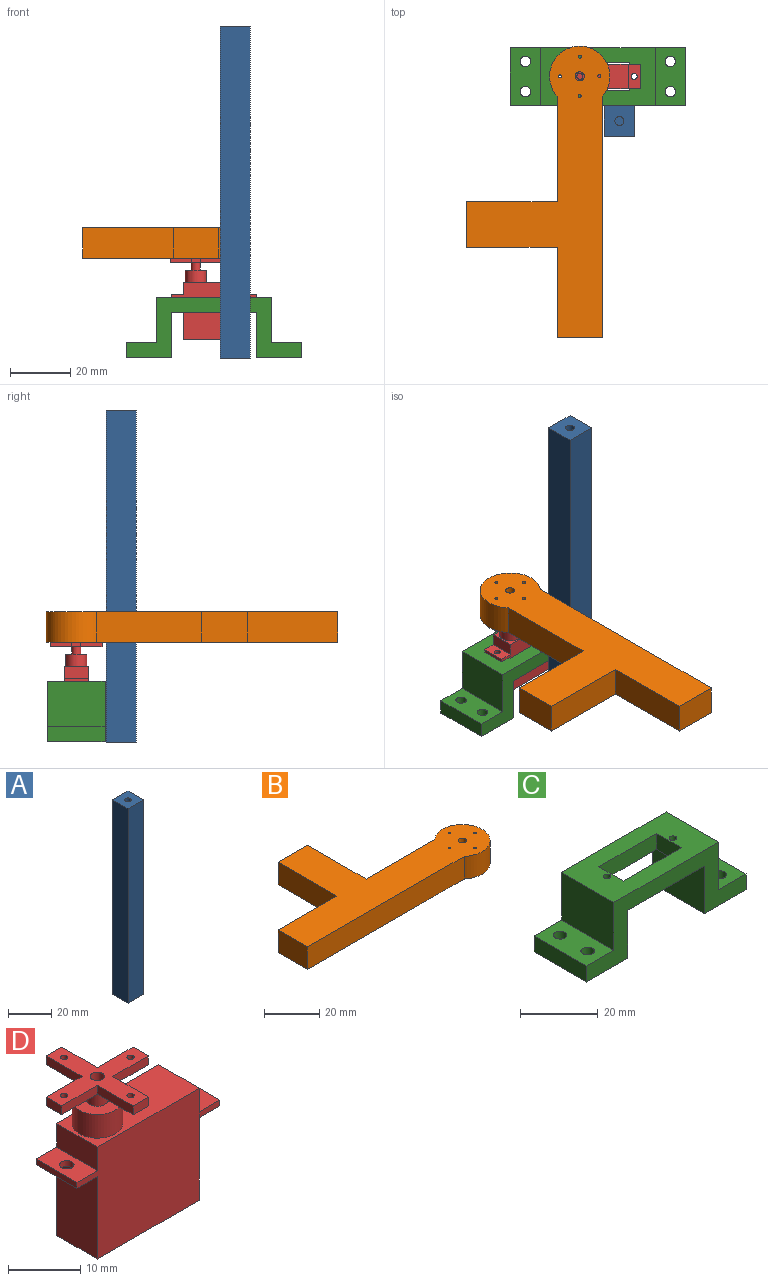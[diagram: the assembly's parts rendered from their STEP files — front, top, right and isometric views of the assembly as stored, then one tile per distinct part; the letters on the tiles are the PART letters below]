
ASSEMBLY  parts=4 mates=2
PART A: 10 faces, bbox 10x10x110 mm
  f0: plane 110x10mm, normal (1,0,0), area 1100mm2, adj f1,f3,f4,f5
  f1: plane 110x10mm, normal (0,1,0), area 1100mm2, adj f0,f2,f4,f5
  f2: plane 110x10mm, normal (-1,0,0), area 1100mm2, adj f1,f3,f4,f5
  f3: plane 110x10mm, normal (0,-1,0), area 1100mm2, adj f0,f2,f4,f5
  f4: plane 10x10mm, normal (0,0,1), area 92.9mm2, adj f0,f1,f2,f3,f8
  f5: plane 10x10mm, normal (0,0,-1), area 92.9mm2, adj f0,f1,f2,f3,f6
  f6: cylinder r=1.5mm len=20mm, axis (0,0,-1), area 188.5mm2, adj f5,f7
  f7: plane 3x3mm, normal (0,0,-1), area 7.1mm2, adj f6
  f8: cylinder r=1.5mm len=30mm, axis (0,0,1), area 282.7mm2, adj f4,f9
  f9: plane 3x3mm, normal (0,0,1), area 7.1mm2, adj f8
PART B: 15 faces, bbox 96.6x47.5x10 mm
  f0: cylinder r=10mm len=20mm, axis (0,0,-1), area 458.7mm2, adj f1,f12,f13,f14
  f1: plane 35x10mm, normal (0,1,0), area 350mm2, adj f0,f2,f13,f14
  f2: plane 30x10mm, normal (1,0,0), area 300mm2, adj f1,f3,f13,f14
  f3: plane 15x10mm, normal (0,1,0), area 150mm2, adj f2,f4,f13,f14
  f4: plane 30x10mm, normal (-1,0,0), area 300mm2, adj f3,f5,f13,f14
  f5: plane 30x10mm, normal (0,1,0), area 300mm2, adj f4,f6,f13,f14
  f6: plane 15x10mm, normal (-1,0,0), area 150mm2, adj f5,f12,f13,f14
  f7: cylinder r=1.5mm len=10mm, axis (0,0,-1), area 94.2mm2, adj f13,f14
  f8: cylinder r=0.5mm len=10mm, axis (0,0,-1), area 31.4mm2, adj f13,f14
  f9: cylinder r=0.5mm len=10mm, axis (0,0,-1), area 31.4mm2, adj f13,f14
  f10: cylinder r=0.5mm len=10mm, axis (0,0,-1), area 31.4mm2, adj f13,f14
  f11: cylinder r=0.5mm len=10mm, axis (0,0,-1), area 31.4mm2, adj f13,f14
  f12: plane 80x10mm, normal (0,-1,0), area 800mm2, adj f0,f6,f13,f14
  f13: plane 96.61x47.5mm, normal (0,0,1), area 1918.8mm2, adj f0,f1,f2,f3,f4,f5,f6,f7
  f14: plane 96.61x47.5mm, normal (0,0,-1), area 1918.8mm2, adj f0,f1,f2,f3,f4,f5,f6,f7
PART C: 24 faces, bbox 58x19x20 mm
  f0: plane 28x19mm, normal (0,0,-1), area 336.7mm2, adj f6,f7,f12,f13,f14,f15,f16,f17
  f1: plane 38x19mm, normal (0,0,1), area 526.7mm2, adj f2,f11,f12,f13,f14,f15,f16,f17
  f2: plane 19x15mm, normal (-1,0,0), area 285mm2, adj f1,f3,f12,f13
  f3: plane 19x10mm, normal (0,0,1), area 170.8mm2, adj f2,f4,f12,f13,f22,f23
  f4: plane 19x5mm, normal (-1,0,0), area 95mm2, adj f3,f5,f12,f13
  f5: plane 19x15mm, normal (0,0,-1), area 265.8mm2, adj f4,f6,f12,f13,f22,f23
  f6: plane 19x15mm, normal (1,0,0), area 285mm2, adj f0,f5,f12,f13
  f7: plane 19x15mm, normal (-1,0,0), area 285mm2, adj f0,f8,f12,f13
  f8: plane 19x15mm, normal (0,0,-1), area 265.8mm2, adj f7,f9,f12,f13,f20,f21
  f9: plane 19x5mm, normal (1,0,0), area 95mm2, adj f8,f10,f12,f13
  f10: plane 19x10mm, normal (0,0,1), area 170.8mm2, adj f9,f11,f12,f13,f20,f21
  f11: plane 19x15mm, normal (1,0,0), area 285mm2, adj f1,f10,f12,f13
  f12: plane 58x20mm, normal (0,-1,0), area 440mm2, adj f0,f1,f2,f3,f4,f5,f6,f7
  f13: plane 58x20mm, normal (0,1,0), area 440mm2, adj f0,f1,f2,f3,f4,f5,f6,f7
  f14: plane 9x5mm, normal (-1,0,0), area 45mm2, adj f0,f1,f15,f17
  f15: plane 21x5mm, normal (0,-1,0), area 105mm2, adj f0,f1,f14,f16
  f16: plane 9x5mm, normal (1,0,0), area 45mm2, adj f0,f1,f15,f17
  f17: plane 21x5mm, normal (0,1,0), area 105mm2, adj f0,f1,f14,f16
  f18: cylinder r=1mm len=5mm, axis (0,0,1), area 31.4mm2, adj f0,f1
  f19: cylinder r=1mm len=5mm, axis (0,0,1), area 31.4mm2, adj f0,f1
  f20: cylinder r=1.75mm len=5mm, axis (0,0,1), area 55mm2, adj f8,f10
  f21: cylinder r=1.75mm len=5mm, axis (0,0,1), area 55mm2, adj f8,f10
  f22: cylinder r=1.75mm len=5mm, axis (0,0,1), area 55mm2, adj f3,f5
  f23: cylinder r=1.75mm len=5mm, axis (0,0,1), area 55mm2, adj f3,f5
PART D: 41 faces, bbox 28.5x17x27 mm
  f0: plane 8x4mm, normal (-1,0,0), area 32mm2, adj f3,f5,f6,f16
  f1: plane 14x8mm, normal (1,0,0), area 112mm2, adj f3,f5,f7,f11
  f2: plane 14x8mm, normal (-1,0,0), area 112mm2, adj f3,f5,f7,f15
  f3: plane 24x19mm, normal (0,-1,0), area 384mm2, adj f0,f1,f2,f4,f6,f7,f10,f15
  f4: plane 8x4mm, normal (1,0,0), area 32mm2, adj f3,f5,f6,f13
  f5: plane 24x19mm, normal (0,1,0), area 384mm2, adj f0,f1,f2,f4,f6,f7,f12,f15
  f6: plane 20x8mm, normal (0,0,1), area 121.5mm2, adj f0,f3,f4,f5,f8
  f7: plane 20x8mm, normal (0,0,-1), area 160mm2, adj f1,f2,f3,f5
  f8: cylinder r=3.5mm len=7mm, axis (0,0,-1), area 88mm2, adj f6,f9
  f9: plane 7x7mm, normal (0,0,1), area 31.4mm2, adj f8,f18
  f10: plane 4x1mm, normal (0,-1,0), area 4mm2, adj f3,f11,f13,f14
  f11: plane 8x4mm, normal (0,0,-1), area 28.9mm2, adj f1,f10,f12,f14,f20
  f12: plane 4x1mm, normal (0,1,0), area 4mm2, adj f5,f11,f13,f14
  f13: plane 8x4mm, normal (0,0,1), area 28.9mm2, adj f4,f10,f12,f14,f20
  f14: plane 8x1mm, normal (1,0,0), area 8mm2, adj f10,f11,f12,f13
  f15: plane 8x4mm, normal (0,0,-1), area 28.9mm2, adj f2,f3,f5,f17,f19
  f16: plane 8x4mm, normal (0,0,1), area 28.9mm2, adj f0,f3,f5,f17,f19
  f17: plane 8x1mm, normal (-1,0,0), area 8mm2, adj f3,f5,f15,f16
  f18: cylinder r=1.5mm len=3mm, axis (0,0,-1), area 23.6mm2, adj f9,f34
  f19: cylinder r=1mm len=2mm, axis (0,0,1), area 6.3mm2, adj f15,f16
  f20: cylinder r=1mm len=2mm, axis (0,0,1), area 6.3mm2, adj f11,f13
  f21: plane 7x1.5mm, normal (0,1,0), area 10.5mm2, adj f22,f32,f33,f34
  f22: plane 3x1.5mm, normal (-1,0,0), area 4.5mm2, adj f21,f23,f33,f34
  f23: plane 7x1.5mm, normal (0,-1,0), area 10.5mm2, adj f22,f24,f33,f34
  f24: plane 7x1.5mm, normal (-1,0,0), area 10.5mm2, adj f23,f25,f33,f34
  f25: plane 3x1.5mm, normal (0,-1,0), area 4.5mm2, adj f24,f26,f33,f34
  f26: plane 7x1.5mm, normal (1,0,0), area 10.5mm2, adj f25,f27,f33,f34
  f27: plane 7x1.5mm, normal (0,-1,0), area 10.5mm2, adj f26,f28,f33,f34
  f28: plane 3x1.5mm, normal (1,0,0), area 4.5mm2, adj f27,f29,f33,f34
  f29: plane 7x1.5mm, normal (0,1,0), area 10.5mm2, adj f28,f30,f33,f34
  f30: plane 7x1.5mm, normal (1,0,0), area 10.5mm2, adj f29,f31,f33,f34
  f31: plane 3x1.5mm, normal (0,1,0), area 4.5mm2, adj f30,f32,f33,f34
  f32: plane 7x1.5mm, normal (-1,0,0), area 10.5mm2, adj f21,f31,f33,f34
  f33: plane 17x17mm, normal (0,0,1), area 86.7mm2, adj f21,f22,f23,f24,f25,f26,f27,f28
  f34: plane 17x17mm, normal (0,0,-1), area 82.8mm2, adj f18,f21,f22,f23,f24,f25,f26,f27
  f35: cylinder r=0.5mm len=1.5mm, axis (0,0,1), area 4.7mm2, adj f33,f34
  f36: cylinder r=0.5mm len=1.5mm, axis (0,0,1), area 4.7mm2, adj f33,f34
  f37: cylinder r=0.5mm len=1.5mm, axis (0,0,1), area 4.7mm2, adj f33,f34
  f38: cylinder r=0.5mm len=1.5mm, axis (0,0,1), area 4.7mm2, adj f33,f34
  f39: cylinder r=1mm len=2mm, axis (0,0,1), area 12.6mm2, adj f33,f40
  f40: plane 2x2mm, normal (0,0,1), area 3.1mm2, adj f39
PLACE A t=(7.11,-24.42,-17.61)mm
PLACE B rot(axis=(0,0,1),90deg) t=(-6,-9.5,15.5)mm
PLACE C at identity fixed
PLACE D t=(11.75,-3.7,-11.5)mm
MATE revolute B.f0 <-> D.f8  axis (0,0,-1) through (-6,-9.5,15.5)mm
MATE fastened D.f20 <-> C.f18  axis (0,0,-1) through (12,-9.5,2.5)mm
